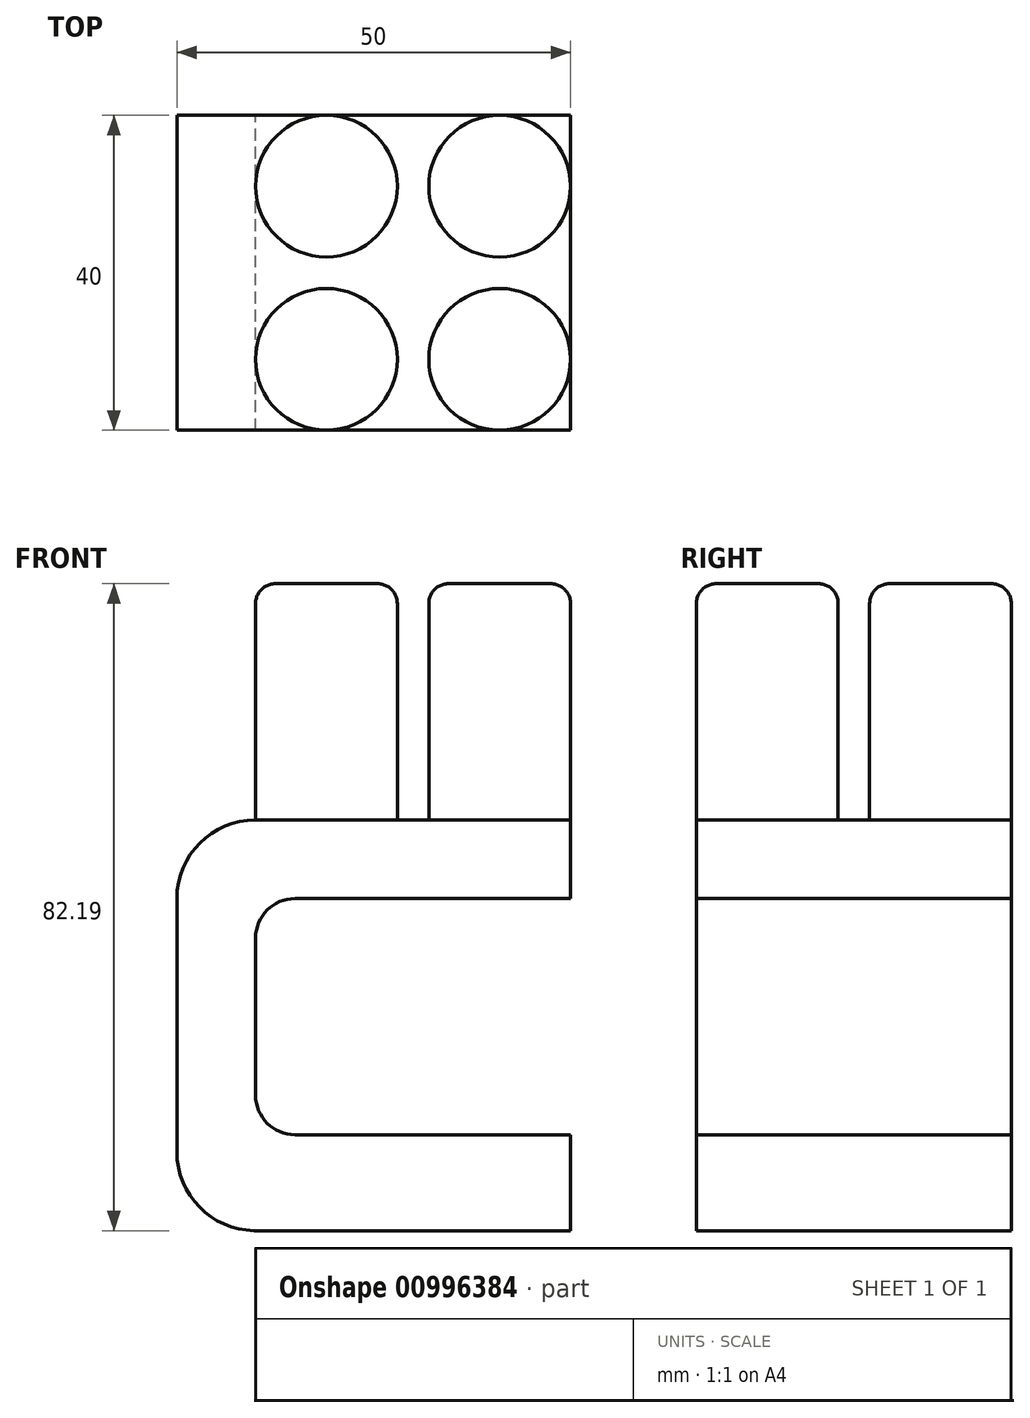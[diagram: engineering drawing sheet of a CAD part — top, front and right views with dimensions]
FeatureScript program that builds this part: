
annotation { "Feature Type Name" : "Feature", "Feature Type Description" : "" }
export const myFeature = defineFeature(function(context is Context, id is Id, definition is map)
    precondition{}
    {
        {
            var Q0;
            Q0=qCreatedBy(makeId("Front.planeOp"),FACE);
            var sketch = newSketch(context, id + "F0", { "sketchPlane" : qUnion([Q0])});
            skLineSegment(sketch, "E0.bottom", {"start": v(20, -5) * mm, "end": v(-10, -5) * mm});
            skLineSegment(sketch, "E0.top", {"start": v(20, 5) * mm, "end": v(-20, 5) * mm});
            skLineSegment(sketch, "E0.left", {"start": v(20, -5) * mm, "end": v(20, 5) * mm});
            skPoint(sketch, "E0.middle", {"position": v(0, 0) * mm});
            skLineSegment(sketch, "E1.top", {"start": v(-20, 5) * mm, "end": v(-20, 5) * mm});
            skLineSegment(sketch, "E1.right", {"start": v(-30, -5) * mm, "end": v(-30, -5) * mm});
            skPoint(sketch, "E1.middle", {"position": v(-25, 0) * mm});
            skPoint(sketch, "E2.visualSharp", {"position": v(-30, 5) * mm});
            skArc(sketch, "E2.filletArc", {"start": v(-20, 5) * mm, "mid": v(-27.07, 2.07) * mm, "end": v(-30, -5) * mm});
            skLineSegment(sketch, "E3", {"start": v(0, -5) * mm, "end": v(0, -25) * mm, "construction": true});
            skLineSegment(sketch, "E4", {"start": v(-30, -5) * mm, "end": v(-30, -37) * mm});
            skLineSegment(sketch, "E5", {"start": v(-20, -15) * mm, "end": v(-20, -30) * mm});
            skLineSegment(sketch, "E6", {"start": v(-10, -5) * mm, "end": v(-15, -5) * mm});
            skLineSegment(sketch, "E7", {"start": v(-20, -15) * mm, "end": v(-20, -10) * mm});
            skArc(sketch, "E8.filletArc", {"start": v(-15, -5) * mm, "mid": v(-18.54, -6.46) * mm, "end": v(-20, -10) * mm});
            skLineSegment(sketch, "E9.bottom", {"start": v(-48.31, -24.83) * mm, "end": v(-58.31, -24.83) * mm});
            skLineSegment(sketch, "E9.top", {"start": v(-48.31, -14.83) * mm, "end": v(-58.31, -14.83) * mm});
            skLineSegment(sketch, "E9.left", {"start": v(-48.31, -24.83) * mm, "end": v(-48.31, -14.83) * mm});
            skLineSegment(sketch, "E9.right", {"start": v(-58.31, -24.83) * mm, "end": v(-58.31, -14.83) * mm});
            skPoint(sketch, "E9.middle", {"position": v(-53.31, -19.83) * mm});
            skLineSegment(sketch, "E10.bottom", {"start": v(-20, -47.2) * mm, "end": v(-20.18, -47.19) * mm});
            skLineSegment(sketch, "E10.right", {"start": v(-30, -37.2) * mm, "end": v(-30, -37) * mm});
            skPoint(sketch, "E10.middle", {"position": v(-25, -42.1) * mm});
            skPoint(sketch, "E11.visualSharp", {"position": v(-30, -47) * mm});
            skArc(sketch, "E11.filletArc", {"start": v(-30, -37.2) * mm, "mid": v(-27.13, -44.2) * mm, "end": v(-20.18, -47.19) * mm});
            skPoint(sketch, "E12.visualSharp", {"position": v(-20, -37) * mm});
            skArc(sketch, "E12.filletArc", {"start": v(-20, -30) * mm, "mid": v(-18.54, -33.54) * mm, "end": v(-15, -35) * mm});
            skLineSegment(sketch, "E13", {"start": v(20, -5) * mm, "end": v(20, -55.78) * mm, "construction": true});
            skLineSegment(sketch, "E14", {"start": v(-20, -47.2) * mm, "end": v(20, -47.2) * mm});
            skLineSegment(sketch, "E15", {"start": v(-15, -35) * mm, "end": v(20, -35) * mm});
            skLineSegment(sketch, "E16", {"start": v(20, -35) * mm, "end": v(20, -47.2) * mm});
            skSolve(sketch);
        }
        {
            var Q0;
            Q0=makeQuery(id+"F0.imprint","IMPRINT",FACE,{"disambiguationData":[TD([[makeQuery(id+"F0.imprint","IMPRINT",EDGE,{"derivedFrom":sQuery(id+"F0.wireOp",EDGE,"E0.bottom")}),-1.0]])]});
            var Q1;
            Q1=makeQuery(id+"F0.imprint","IMPRINT",FACE,{"disambiguationData":[TD([[makeQuery(id+"F0.imprint","IMPRINT",EDGE,{"derivedFrom":sQuery(id+"F0.wireOp",EDGE,"f48320ab-85e9-42ec-91e9-b24312025075.right")}),-1.0]])]});
            var Q2;
            Q2=makeQuery(id+"F0.imprint","IMPRINT",FACE,{"disambiguationData":[TD([[makeQuery(id+"F0.imprint","IMPRINT",EDGE,{"derivedFrom":sQuery(id+"F0.wireOp",EDGE,"17ae7206-6f2c-45b5-895e-0083e8836de8.bottom")}),-1.0]])]});
            var Q3;
            Q3=makeQuery(id+"F0.imprint","IMPRINT",FACE,{"disambiguationData":[TD([[makeQuery(id+"F0.imprint","IMPRINT",EDGE,{"derivedFrom":sQuery(id+"F0.wireOp",EDGE,"805abf84-5688-4cf1-8da6-7f429852980b.bottom")}),-1.0]])]});
            extrude(context, id + "F1", {"entities" : qUnion([Q0, Q1, Q2, Q3]), "endBound" : BoundingType.SYMMETRIC, "depth" : 40 * mm, "offsetDistance" : 25 * mm});
        }
        {
            var Q0;
            Q0=makeQuery(id+"F1.opExtrude","SWEPT_FACE",FACE,{"disambiguationData":[OSD([sQuery(id+"F0.wireOp",EDGE,"E0.top")])]});
            var sketch = newSketch(context, id + "F2", { "sketchPlane" : qUnion([Q0])});
            skLineSegment(sketch, "E17.left", {"start": v(0, -20) * mm, "end": v(0, 20) * mm});
            skLineSegment(sketch, "E18.top", {"start": v(42.29, 57.77) * mm, "end": v(44.29, 57.77) * mm});
            skPoint(sketch, "E18.middle", {"position": v(43.29, 37.77) * mm});
            skLineSegment(sketch, "E19", {"start": v(0, 20) * mm, "end": v(-2, 20) * mm});
            skLineSegment(sketch, "E20", {"start": v(-2, 20) * mm, "end": v(-2, -20) * mm});
            skLineSegment(sketch, "E21", {"start": v(-2, -20) * mm, "end": v(0, -20) * mm});
            skLineSegment(sketch, "E22", {"start": v(0, 20) * mm, "end": v(2, 20) * mm});
            skLineSegment(sketch, "E23", {"start": v(2, 20) * mm, "end": v(2, -20) * mm});
            skLineSegment(sketch, "E24", {"start": v(2, -20) * mm, "end": v(0, -20) * mm});
            skLineSegment(sketch, "E25", {"start": v(-20, 0) * mm, "end": v(20, 0) * mm});
            skLineSegment(sketch, "E26", {"start": v(20, 0) * mm, "end": v(20, 2) * mm});
            skLineSegment(sketch, "E27", {"start": v(20, 2) * mm, "end": v(-20, 2) * mm});
            skLineSegment(sketch, "E28", {"start": v(-20, 2) * mm, "end": v(-20, 0) * mm});
            skLineSegment(sketch, "E29", {"start": v(-20, 0) * mm, "end": v(-20, -2) * mm});
            skLineSegment(sketch, "E30", {"start": v(-20, -2) * mm, "end": v(20, -2) * mm});
            skLineSegment(sketch, "E31", {"start": v(20, -2) * mm, "end": v(20, 0) * mm});
            skLineSegment(sketch, "E32", {"start": v(11, 20) * mm, "end": v(11, -20) * mm});
            skLineSegment(sketch, "E33", {"start": v(11, 20) * mm, "end": v(20, 20) * mm});
            skLineSegment(sketch, "E34", {"start": v(-11, 20) * mm, "end": v(-11, -20) * mm});
            skLineSegment(sketch, "E35", {"start": v(-11, -20) * mm, "end": v(-20, -20) * mm});
            skLineSegment(sketch, "E36", {"start": v(-20, 11) * mm, "end": v(20, 11) * mm});
            skLineSegment(sketch, "E37", {"start": v(20, 11) * mm, "end": v(20, 20) * mm});
            skLineSegment(sketch, "E38", {"start": v(-20, -11) * mm, "end": v(20, -11) * mm});
            skLineSegment(sketch, "E39", {"start": v(20, -11) * mm, "end": v(20, -20) * mm});
            skCircle(sketch, "E40", {"center": v(11, 11) * mm, "radius": 9 * mm});
            skCircle(sketch, "E41", {"center": v(11, -11) * mm, "radius": 9 * mm});
            skCircle(sketch, "E42", {"center": v(-11, -11) * mm, "radius": 9 * mm});
            skCircle(sketch, "E43", {"center": v(-11, 11) * mm, "radius": 9 * mm});
            skSolve(sketch);
        }
        {
            var Q0;
            {var subQ1=sQuery(id+"F2.wireOp",EDGE,"E34");var subQ3=sQuery(id+"F2.wireOp",EDGE,"E36");var subQ4=makeQuery(id+"F2.imprint","INTERSECT",VERTEX,{"derivedFrom":[subQ1,subQ3]});Q0=makeQuery(id+"F2.imprint","IMPRINT",FACE,{"disambiguationData":[TD([[makeQuery(id+"F2.imprint","IMPRINT",EDGE,{"disambiguationData":[TD([[subQ4,1.0]])],"derivedFrom":subQ1}),1.0]])]});}
            var Q1;
            {var subQ1=sQuery(id+"F2.wireOp",EDGE,"E34");var subQ4=sQuery(id+"F2.wireOp",EDGE,"E36");var subQ5=makeQuery(id+"F2.imprint","INTERSECT",VERTEX,{"derivedFrom":[subQ1,subQ4]});Q1=makeQuery(id+"F2.imprint","IMPRINT",FACE,{"disambiguationData":[TD([[makeQuery(id+"F2.imprint","IMPRINT",EDGE,{"disambiguationData":[TD([[subQ5,1.0]])],"derivedFrom":subQ1}),-1.0]])]});}
            var Q2;
            {var subQ0=sQuery(id+"F2.wireOp",EDGE,"E36");var subQ1=sQuery(id+"F2.wireOp",EDGE,"E34");var subQ2=makeQuery(id+"F2.imprint","INTERSECT",VERTEX,{"derivedFrom":[subQ1,subQ0]});Q2=makeQuery(id+"F2.imprint","IMPRINT",FACE,{"disambiguationData":[TD([[makeQuery(id+"F2.imprint","IMPRINT",EDGE,{"disambiguationData":[TD([[subQ2,-1.0]])],"derivedFrom":subQ1}),-1.0]])]});}
            var Q3;
            {var subQ0=sQuery(id+"F2.wireOp",EDGE,"E36");var subQ1=sQuery(id+"F2.wireOp",EDGE,"E34");var subQ2=makeQuery(id+"F2.imprint","INTERSECT",VERTEX,{"derivedFrom":[subQ1,subQ0]});Q3=makeQuery(id+"F2.imprint","IMPRINT",FACE,{"disambiguationData":[TD([[makeQuery(id+"F2.imprint","IMPRINT",EDGE,{"disambiguationData":[TD([[subQ2,-1.0]])],"derivedFrom":subQ1}),1.0]])]});}
            var Q4;
            {var subQ1=sQuery(id+"F2.wireOp",EDGE,"E32");var subQ3=sQuery(id+"F2.wireOp",EDGE,"E36");var subQ4=makeQuery(id+"F2.imprint","INTERSECT",VERTEX,{"derivedFrom":[subQ1,subQ3]});Q4=makeQuery(id+"F2.imprint","IMPRINT",FACE,{"disambiguationData":[TD([[makeQuery(id+"F2.imprint","IMPRINT",EDGE,{"disambiguationData":[TD([[subQ4,1.0]])],"derivedFrom":subQ3}),1.0]])]});}
            var Q5;
            {var subQ1=sQuery(id+"F2.wireOp",EDGE,"E32");var subQ4=sQuery(id+"F2.wireOp",EDGE,"E36");var subQ5=makeQuery(id+"F2.imprint","INTERSECT",VERTEX,{"derivedFrom":[subQ1,subQ4]});Q5=makeQuery(id+"F2.imprint","IMPRINT",FACE,{"disambiguationData":[TD([[makeQuery(id+"F2.imprint","IMPRINT",EDGE,{"disambiguationData":[TD([[subQ5,1.0]])],"derivedFrom":subQ1}),1.0]])]});}
            var Q6;
            {var subQ0=sQuery(id+"F2.wireOp",EDGE,"E36");var subQ1=sQuery(id+"F2.wireOp",EDGE,"E32");var subQ2=makeQuery(id+"F2.imprint","INTERSECT",VERTEX,{"derivedFrom":[subQ1,subQ0]});Q6=makeQuery(id+"F2.imprint","IMPRINT",FACE,{"disambiguationData":[TD([[makeQuery(id+"F2.imprint","IMPRINT",EDGE,{"disambiguationData":[TD([[subQ2,-1.0]])],"derivedFrom":subQ1}),1.0]])]});}
            var Q7;
            {var subQ0=sQuery(id+"F2.wireOp",EDGE,"E36");var subQ1=sQuery(id+"F2.wireOp",EDGE,"E32");var subQ2=makeQuery(id+"F2.imprint","INTERSECT",VERTEX,{"derivedFrom":[subQ1,subQ0]});Q7=makeQuery(id+"F2.imprint","IMPRINT",FACE,{"disambiguationData":[TD([[makeQuery(id+"F2.imprint","IMPRINT",EDGE,{"disambiguationData":[TD([[subQ2,-1.0]])],"derivedFrom":subQ1}),-1.0]])]});}
            var Q8;
            {var subQ0=sQuery(id+"F2.wireOp",EDGE,"E38");var subQ1=sQuery(id+"F2.wireOp",EDGE,"E32");var subQ2=makeQuery(id+"F2.imprint","INTERSECT",VERTEX,{"derivedFrom":[subQ1,subQ0]});Q8=makeQuery(id+"F2.imprint","IMPRINT",FACE,{"disambiguationData":[TD([[makeQuery(id+"F2.imprint","IMPRINT",EDGE,{"disambiguationData":[TD([[subQ2,1.0]])],"derivedFrom":subQ1}),-1.0]])]});}
            var Q9;
            {var subQ0=sQuery(id+"F2.wireOp",EDGE,"E38");var subQ1=sQuery(id+"F2.wireOp",EDGE,"E32");var subQ2=makeQuery(id+"F2.imprint","INTERSECT",VERTEX,{"derivedFrom":[subQ1,subQ0]});Q9=makeQuery(id+"F2.imprint","IMPRINT",FACE,{"disambiguationData":[TD([[makeQuery(id+"F2.imprint","IMPRINT",EDGE,{"disambiguationData":[TD([[subQ2,1.0]])],"derivedFrom":subQ1}),1.0]])]});}
            var Q10;
            {var subQ1=sQuery(id+"F2.wireOp",EDGE,"E32");var subQ4=sQuery(id+"F2.wireOp",EDGE,"E38");var subQ5=makeQuery(id+"F2.imprint","INTERSECT",VERTEX,{"derivedFrom":[subQ1,subQ4]});Q10=makeQuery(id+"F2.imprint","IMPRINT",FACE,{"disambiguationData":[TD([[makeQuery(id+"F2.imprint","IMPRINT",EDGE,{"disambiguationData":[TD([[subQ5,-1.0]])],"derivedFrom":subQ1}),1.0]])]});}
            var Q11;
            {var subQ1=sQuery(id+"F2.wireOp",EDGE,"E32");var subQ3=sQuery(id+"F2.wireOp",EDGE,"E38");var subQ4=makeQuery(id+"F2.imprint","INTERSECT",VERTEX,{"derivedFrom":[subQ1,subQ3]});Q11=makeQuery(id+"F2.imprint","IMPRINT",FACE,{"disambiguationData":[TD([[makeQuery(id+"F2.imprint","IMPRINT",EDGE,{"disambiguationData":[TD([[subQ4,-1.0]])],"derivedFrom":subQ1}),-1.0]])]});}
            var Q12;
            {var subQ1=sQuery(id+"F2.wireOp",EDGE,"E34");var subQ3=sQuery(id+"F2.wireOp",EDGE,"E38");var subQ4=makeQuery(id+"F2.imprint","INTERSECT",VERTEX,{"derivedFrom":[subQ1,subQ3]});Q12=makeQuery(id+"F2.imprint","IMPRINT",FACE,{"disambiguationData":[TD([[makeQuery(id+"F2.imprint","IMPRINT",EDGE,{"disambiguationData":[TD([[subQ4,-1.0]])],"derivedFrom":subQ3}),-1.0]])]});}
            var Q13;
            {var subQ1=sQuery(id+"F2.wireOp",EDGE,"E34");var subQ4=sQuery(id+"F2.wireOp",EDGE,"E38");var subQ5=makeQuery(id+"F2.imprint","INTERSECT",VERTEX,{"derivedFrom":[subQ1,subQ4]});Q13=makeQuery(id+"F2.imprint","IMPRINT",FACE,{"disambiguationData":[TD([[makeQuery(id+"F2.imprint","IMPRINT",EDGE,{"disambiguationData":[TD([[subQ5,-1.0]])],"derivedFrom":subQ1}),-1.0]])]});}
            var Q14;
            {var subQ0=sQuery(id+"F2.wireOp",EDGE,"E38");var subQ1=sQuery(id+"F2.wireOp",EDGE,"E34");var subQ2=makeQuery(id+"F2.imprint","INTERSECT",VERTEX,{"derivedFrom":[subQ1,subQ0]});Q14=makeQuery(id+"F2.imprint","IMPRINT",FACE,{"disambiguationData":[TD([[makeQuery(id+"F2.imprint","IMPRINT",EDGE,{"disambiguationData":[TD([[subQ2,1.0]])],"derivedFrom":subQ1}),-1.0]])]});}
            var Q15;
            {var subQ0=sQuery(id+"F2.wireOp",EDGE,"E38");var subQ1=sQuery(id+"F2.wireOp",EDGE,"E34");var subQ2=makeQuery(id+"F2.imprint","INTERSECT",VERTEX,{"derivedFrom":[subQ1,subQ0]});Q15=makeQuery(id+"F2.imprint","IMPRINT",FACE,{"disambiguationData":[TD([[makeQuery(id+"F2.imprint","IMPRINT",EDGE,{"disambiguationData":[TD([[subQ2,1.0]])],"derivedFrom":subQ1}),1.0]])]});}
            extrude(context, id + "F3", {"entities" : qUnion([Q0, Q1, Q2, Q3, Q4, Q5, Q6, Q7, Q8, Q9, Q10, Q11, Q12, Q13, Q14, Q15]), "operationType" : NewBodyOperationType.ADD, "depth" : 30 * mm, "offsetDistance" : 25 * mm});
        }
        {
            var Q0;
            Q0=makeQuery(id+"F3.opExtrude","CAP_FACE",FACE,{"disambiguationData":[OSD([sQuery(id+"F2.wireOp",EDGE,"E43")])],"isStart":false});
            var Q1;
            Q1=makeQuery(id+"F3.opExtrude","CAP_FACE",FACE,{"disambiguationData":[OSD([sQuery(id+"F2.wireOp",EDGE,"E40")])],"isStart":false});
            var Q2;
            Q2=makeQuery(id+"F3.opExtrude","CAP_FACE",FACE,{"disambiguationData":[OSD([sQuery(id+"F2.wireOp",EDGE,"E41")])],"isStart":false});
            var Q3;
            Q3=makeQuery(id+"F3.opExtrude","CAP_FACE",FACE,{"disambiguationData":[OSD([sQuery(id+"F2.wireOp",EDGE,"E42")])],"isStart":false});
            fillet(context, id + "F4", {"entities" : qUnion([Q0, Q1, Q2, Q3]), "radius" : 2.5 * mm, "tangentPropagation" : true, "allowEdgeOverflow" : false});
        }
    });
